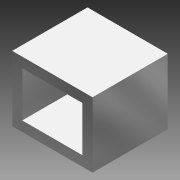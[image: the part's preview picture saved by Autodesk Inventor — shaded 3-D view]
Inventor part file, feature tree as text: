
AUTODESK INVENTOR PART (.ipt)
format: ipt  version: 2013 SP1 (Build 170176100, 176)  size: 98,304 bytes
history: native  units: mm
features: extrude x1, shell x1, sketch x1
ambient origin geometry x8: Origin, YZ Plane, XZ Plane, XY Plane, X Axis, Y Axis, Z Axis, Center Point
bodies: Volumenkörper1 (feature_tree)
feature tree (3):
  extrude  "Extrusion1"  Depth=15.0mm
  shell  "Wandstärke1"  Thickness=13.0mm
  sketch  "Skizze1"  dims[d0=16.0mm d1=15.0mm d2=13.0mm d3=0.0mm d4=2.0mm]
